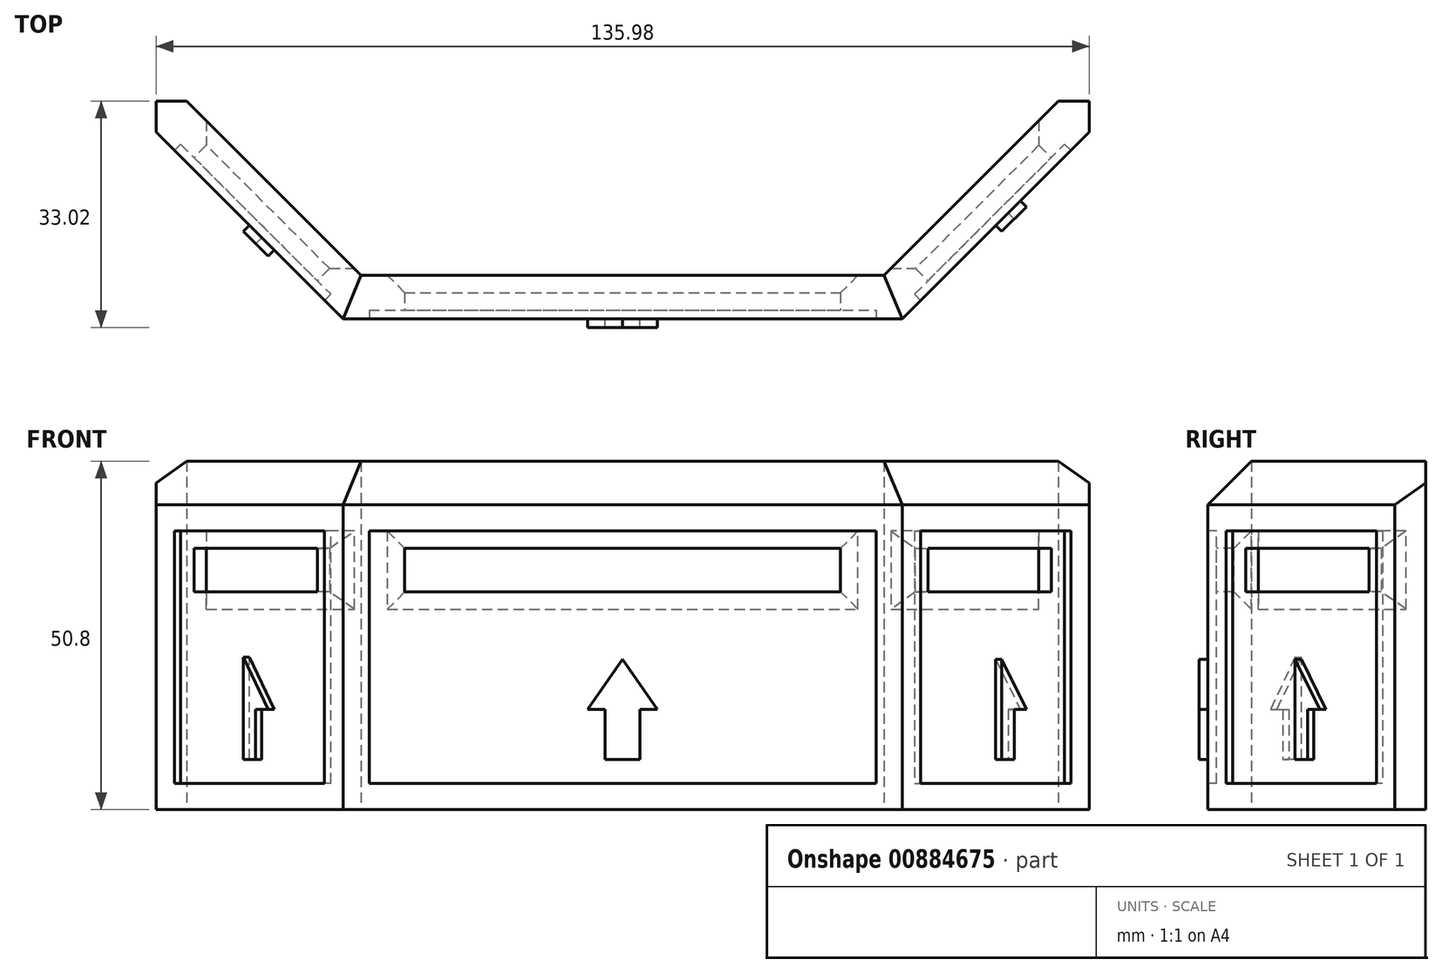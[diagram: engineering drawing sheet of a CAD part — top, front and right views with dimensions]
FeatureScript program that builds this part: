
annotation { "Feature Type Name" : "Feature", "Feature Type Description" : "" }
export const myFeature = defineFeature(function(context is Context, id is Id, definition is map)
    precondition{}
    {
        {
            var Q0;
            Q0=qCreatedBy(makeId("Top.planeOp"),FACE);
            var sketch = newSketch(context, id + "F0", { "sketchPlane" : qUnion([Q0])});
            skLineSegment(sketch, "E0", {"start": v(38.1, 0) * mm, "end": v(-38.1, 0) * mm});
            skLineSegment(sketch, "E1", {"start": v(-38.1, 0) * mm, "end": v(-63.5, 25.4) * mm});
            skLineSegment(sketch, "E2", {"start": v(38.1, 0) * mm, "end": v(63.5, 25.4) * mm});
            skPoint(sketch, "E3.start.orphan", {"position": v(0, 0) * mm});
            skLineSegment(sketch, "E4.0", {"start": v(42.6, -4.5) * mm, "end": v(68, 20.9) * mm});
            skLineSegment(sketch, "E5.0", {"start": v(-42.6, -4.5) * mm, "end": v(-68, 20.9) * mm});
            skLineSegment(sketch, "E6", {"start": v(-42.6, -4.5) * mm, "end": v(-40.73, -6.35) * mm});
            skLineSegment(sketch, "E7", {"start": v(-38.1, -6.35) * mm, "end": v(-40.73, -6.35) * mm});
            skLineSegment(sketch, "E8", {"start": v(-38.1, -6.35) * mm, "end": v(40.73, -6.35) * mm});
            skLineSegment(sketch, "E9", {"start": v(42.6, -4.5) * mm, "end": v(40.73, -6.35) * mm});
            skLineSegment(sketch, "E10", {"start": v(-68, 20.9) * mm, "end": v(-68, 25.4) * mm});
            skLineSegment(sketch, "E11", {"start": v(-63.5, 25.4) * mm, "end": v(-68, 25.4) * mm});
            skLineSegment(sketch, "E12", {"start": v(-68, 25.4) * mm, "end": v(-63.5, 25.4) * mm});
            skLineSegment(sketch, "E13", {"start": v(68, 20.9) * mm, "end": v(68, 25.4) * mm});
            skLineSegment(sketch, "E14.trimOffspring", {"start": v(63.5, 25.4) * mm, "end": v(68, 25.4) * mm});
            skSolve(sketch);
        }
        {
            var Q0;
            Q0=qSketchRegion(id+"F0",true);
            extrude(context, id + "F1", {"entities" : qUnion([Q0]), "depth" : 50.8 * mm, "offsetDistance" : 25.4 * mm});
        }
        {
            var Q0;
            Q0=makeQuery(id+"F1.opExtrude","CAP_EDGE",EDGE,{"disambiguationData":[OSD([sQuery(id+"F0.wireOp",EDGE,"E5.0"),sQuery(id+"F0.wireOp",EDGE,"E6")])],"isStart":false});
            var Q1;
            Q1=makeQuery(id+"F1.opExtrude","CAP_EDGE",EDGE,{"disambiguationData":[OSD([sQuery(id+"F0.wireOp",EDGE,"E7"),sQuery(id+"F0.wireOp",EDGE,"E8")])],"isStart":false});
            var Q2;
            Q2=makeQuery(id+"F1.opExtrude","CAP_EDGE",EDGE,{"disambiguationData":[OSD([sQuery(id+"F0.wireOp",EDGE,"E4.0"),sQuery(id+"F0.wireOp",EDGE,"E9")])],"isStart":false});
            chamfer(context, id + "F2", {"entities" : qUnion([Q0, Q1, Q2]), "chamferType" : ChamferType.OFFSET_ANGLE, "width" : 6.35 * mm, "oppositeDirection" : false, "angle" : 45 * degree, "tangentPropagation" : true});
        }
        {
            var Q0;
            Q0=makeQuery(id+"F1.opExtrude","SWEPT_FACE",FACE,{"disambiguationData":[OSD([sQuery(id+"F0.wireOp",EDGE,"E7"),sQuery(id+"F0.wireOp",EDGE,"E8")])]});
            var sketch = newSketch(context, id + "F3", { "sketchPlane" : qUnion([Q0])});
            skLineSegment(sketch, "E15", {"start": v(0, 0) * mm, "end": v(0, 31.75) * mm});
            skLineSegment(sketch, "E16", {"start": v(0, 31.75) * mm, "end": v(31.75, 31.75) * mm});
            skLineSegment(sketch, "E17", {"start": v(31.75, 31.75) * mm, "end": v(-31.75, 31.75) * mm});
            skLineSegment(sketch, "E18", {"start": v(0, 31.75) * mm, "end": v(0, 38.1) * mm});
            skLineSegment(sketch, "E19", {"start": v(0, 38.1) * mm, "end": v(31.75, 38.1) * mm});
            skLineSegment(sketch, "E20", {"start": v(31.75, 38.1) * mm, "end": v(-31.75, 38.1) * mm});
            skLineSegment(sketch, "E21", {"start": v(-31.75, 31.75) * mm, "end": v(-31.75, 38.1) * mm});
            skLineSegment(sketch, "E22", {"start": v(31.75, 31.75) * mm, "end": v(31.75, 38.1) * mm});
            skLineSegment(sketch, "E23", {"start": v(0, 31.75) * mm, "end": v(0, 29.21) * mm});
            skLineSegment(sketch, "E24", {"start": v(0, 29.21) * mm, "end": v(0, 0) * mm});
            skLineSegment(sketch, "E25", {"start": v(0, 14.6) * mm, "end": v(0, 29.21) * mm});
            skLineSegment(sketch, "E26", {"start": v(0, 14.6) * mm, "end": v(0, 0) * mm});
            skLineSegment(sketch, "E27", {"start": v(0, 7.3) * mm, "end": v(-2.54, 7.3) * mm});
            skLineSegment(sketch, "E28", {"start": v(-2.54, 7.3) * mm, "end": v(2.54, 7.3) * mm});
            skLineSegment(sketch, "E29", {"start": v(-2.54, 14.6) * mm, "end": v(-5.08, 14.6) * mm});
            skLineSegment(sketch, "E30", {"start": v(2.54, 14.6) * mm, "end": v(5.08, 14.6) * mm});
            skLineSegment(sketch, "E31", {"start": v(-5.08, 14.6) * mm, "end": v(0, 21.9) * mm});
            skLineSegment(sketch, "E32", {"start": v(0, 21.9) * mm, "end": v(5.08, 14.6) * mm});
            skLineSegment(sketch, "E33", {"start": v(-2.54, 14.6) * mm, "end": v(-2.54, 7.3) * mm});
            skLineSegment(sketch, "E34", {"start": v(2.54, 14.6) * mm, "end": v(2.54, 7.3) * mm});
            skSolve(sketch);
        }
        {
            var Q0;
            {var subQ2=sQuery(id+"F3.wireOp",EDGE,"E18");Q0=makeQuery(id+"F3.imprint","IMPRINT",FACE,{"disambiguationData":[TD([[makeQuery(id+"F3.imprint","IMPRINT",EDGE,{"derivedFrom":subQ2}),-1.0]])]});}
            var Q1;
            {var subQ2=sQuery(id+"F3.wireOp",EDGE,"E18");Q1=makeQuery(id+"F3.imprint","IMPRINT",FACE,{"disambiguationData":[TD([[makeQuery(id+"F3.imprint","IMPRINT",EDGE,{"derivedFrom":subQ2}),1.0]])]});}
            extrude(context, id + "F4", {"entities" : qUnion([Q0, Q1]), "operationType" : NewBodyOperationType.REMOVE, "oppositeDirection" : true, "depth" : 25.4 * mm, "offsetDistance" : 25.4 * mm});
        }
        {
            var Q0;
            Q0=makeQuery(id+"F4.boolean.opBoolean","COPY",EDGE,{"derivedFrom":makeQuery(id+"F4.opExtrude","CAP_EDGE",EDGE,{"disambiguationData":[OSD([sQuery(id+"F3.wireOp",EDGE,"E17")])],"isStart":true})});
            var Q1;
            Q1=makeQuery(id+"F4.boolean.opBoolean","COPY",EDGE,{"derivedFrom":makeQuery(id+"F4.opExtrude","CAP_EDGE",EDGE,{"disambiguationData":[OSD([sQuery(id+"F3.wireOp",EDGE,"E21")])],"isStart":true})});
            var Q2;
            Q2=makeQuery(id+"F4.boolean.opBoolean","COPY",EDGE,{"derivedFrom":makeQuery(id+"F4.opExtrude","CAP_EDGE",EDGE,{"disambiguationData":[OSD([sQuery(id+"F3.wireOp",EDGE,"E20")])],"isStart":true})});
            var Q3;
            Q3=makeQuery(id+"F4.boolean.opBoolean","COPY",EDGE,{"derivedFrom":makeQuery(id+"F4.opExtrude","CAP_EDGE",EDGE,{"disambiguationData":[OSD([sQuery(id+"F3.wireOp",EDGE,"E22")])],"isStart":true})});
            var Q4;
            Q4=makeQuery(id+"F4.boolean.opBoolean","INTERSECT",EDGE,{"derivedFrom":[makeQuery(id+"F1.opExtrude","SWEPT_FACE",FACE,{"disambiguationData":[OSD([sQuery(id+"F0.wireOp",EDGE,"E0")])]}),makeQuery(id+"F4.opExtrude","SWEPT_FACE",FACE,{"disambiguationData":[OSD([sQuery(id+"F3.wireOp",EDGE,"E21")])]})]});
            var Q5;
            Q5=makeQuery(id+"F4.boolean.opBoolean","INTERSECT",EDGE,{"derivedFrom":[makeQuery(id+"F1.opExtrude","SWEPT_FACE",FACE,{"disambiguationData":[OSD([sQuery(id+"F0.wireOp",EDGE,"E0")])]}),makeQuery(id+"F4.opExtrude","SWEPT_FACE",FACE,{"disambiguationData":[OSD([sQuery(id+"F3.wireOp",EDGE,"E20")])]})]});
            var Q6;
            Q6=makeQuery(id+"F4.boolean.opBoolean","INTERSECT",EDGE,{"derivedFrom":[makeQuery(id+"F1.opExtrude","SWEPT_FACE",FACE,{"disambiguationData":[OSD([sQuery(id+"F0.wireOp",EDGE,"E0")])]}),makeQuery(id+"F4.opExtrude","SWEPT_FACE",FACE,{"disambiguationData":[OSD([sQuery(id+"F3.wireOp",EDGE,"E17")])]})]});
            var Q7;
            Q7=makeQuery(id+"F4.boolean.opBoolean","INTERSECT",EDGE,{"derivedFrom":[makeQuery(id+"F1.opExtrude","SWEPT_FACE",FACE,{"disambiguationData":[OSD([sQuery(id+"F0.wireOp",EDGE,"E0")])]}),makeQuery(id+"F4.opExtrude","SWEPT_FACE",FACE,{"disambiguationData":[OSD([sQuery(id+"F3.wireOp",EDGE,"E22")])]})]});
            chamfer(context, id + "F5", {"entities" : qUnion([Q0, Q1, Q2, Q3, Q4, Q5, Q6, Q7]), "width" : 2.54 * mm, "tangentPropagation" : true});
        }
        {
            var Q0;
            Q0=makeQuery(id+"F1.opExtrude","SWEPT_FACE",FACE,{"disambiguationData":[OSD([sQuery(id+"F0.wireOp",EDGE,"E5.0"),sQuery(id+"F0.wireOp",EDGE,"E6")])]});
            var sketch = newSketch(context, id + "F6", { "sketchPlane" : qUnion([Q0])});
            skLineSegment(sketch, "E35", {"start": v(-47.4, 31.75) * mm, "end": v(-30.89, 31.75) * mm});
            skLineSegment(sketch, "E36", {"start": v(-30.89, 31.75) * mm, "end": v(-56.29, 31.75) * mm});
            skLineSegment(sketch, "E37", {"start": v(-30.89, 31.75) * mm, "end": v(-30.89, 38.1) * mm});
            skLineSegment(sketch, "E38", {"start": v(-39.78, 38.1) * mm, "end": v(-30.89, 38.1) * mm});
            skLineSegment(sketch, "E39", {"start": v(-30.89, 38.1) * mm, "end": v(-56.29, 38.1) * mm});
            skLineSegment(sketch, "E40", {"start": v(-56.29, 31.75) * mm, "end": v(-56.29, 38.1) * mm});
            skPoint(sketch, "E41.start.orphan", {"position": v(-43.59, 0) * mm});
            skLineSegment(sketch, "E42", {"start": v(-43.59, 0) * mm, "end": v(-43.59, 44.45) * mm});
            skLineSegment(sketch, "E43", {"start": v(-43.59, 44.45) * mm, "end": v(-43.59, 31.75) * mm});
            skLineSegment(sketch, "E44", {"start": v(-43.59, 31.75) * mm, "end": v(-43.59, 29.21) * mm});
            skLineSegment(sketch, "E45", {"start": v(-43.59, 29.21) * mm, "end": v(-43.59, 0) * mm});
            skLineSegment(sketch, "E46", {"start": v(-43.59, 14.6) * mm, "end": v(-43.59, 29.21) * mm});
            skLineSegment(sketch, "E47", {"start": v(-43.59, 14.6) * mm, "end": v(-43.59, 0) * mm});
            skLineSegment(sketch, "E48", {"start": v(-46.13, 14.6) * mm, "end": v(-48.67, 14.6) * mm});
            skLineSegment(sketch, "E49", {"start": v(-48.67, 14.6) * mm, "end": v(-46.13, 14.6) * mm});
            skLineSegment(sketch, "E50", {"start": v(-43.59, 22.23) * mm, "end": v(-48.67, 14.6) * mm});
            skLineSegment(sketch, "E51", {"start": v(-43.59, 22.23) * mm, "end": v(-38.5, 14.6) * mm});
            skLineSegment(sketch, "E52", {"start": v(-46.13, 14.6) * mm, "end": v(-46.13, 7.3) * mm});
            skLineSegment(sketch, "E53", {"start": v(-38.5, 14.6) * mm, "end": v(-41.05, 14.6) * mm});
            skLineSegment(sketch, "E54", {"start": v(-41.05, 14.6) * mm, "end": v(-41.05, 7.3) * mm});
            skLineSegment(sketch, "E55", {"start": v(-43.59, 7.3) * mm, "end": v(-41.05, 7.3) * mm});
            skLineSegment(sketch, "E56", {"start": v(-41.05, 7.3) * mm, "end": v(-46.13, 7.3) * mm});
            skLineSegment(sketch, "E57.trimOffspring", {"start": v(-41.05, 14.6) * mm, "end": v(-38.5, 14.6) * mm});
            skSolve(sketch);
        }
        {
            var Q0;
            {var subQ1=sQuery(id+"F6.wireOp",EDGE,"E37");Q0=makeQuery(id+"F6.imprint","IMPRINT",FACE,{"disambiguationData":[TD([[makeQuery(id+"F6.imprint","IMPRINT",EDGE,{"derivedFrom":subQ1}),1.0]])]});}
            var Q1;
            {var subQ0=sQuery(id+"F6.wireOp",EDGE,"E40");Q1=makeQuery(id+"F6.imprint","IMPRINT",FACE,{"disambiguationData":[TD([[makeQuery(id+"F6.imprint","IMPRINT",EDGE,{"derivedFrom":subQ0}),-1.0]])]});}
            extrude(context, id + "F7", {"entities" : qUnion([Q0, Q1]), "operationType" : NewBodyOperationType.REMOVE, "oppositeDirection" : true, "depth" : 25.4 * mm, "offsetDistance" : 25.4 * mm});
        }
        {
            var Q0;
            Q0=makeQuery(id+"F7.boolean.opBoolean","COPY",EDGE,{"derivedFrom":makeQuery(id+"F7.opExtrude","CAP_EDGE",EDGE,{"disambiguationData":[OSD([sQuery(id+"F6.wireOp",EDGE,"E39")])],"isStart":true})});
            var Q1;
            Q1=makeQuery(id+"F7.boolean.opBoolean","COPY",EDGE,{"derivedFrom":makeQuery(id+"F7.opExtrude","CAP_EDGE",EDGE,{"disambiguationData":[OSD([sQuery(id+"F6.wireOp",EDGE,"E37")])],"isStart":true})});
            var Q2;
            Q2=makeQuery(id+"F7.boolean.opBoolean","COPY",EDGE,{"derivedFrom":makeQuery(id+"F7.opExtrude","CAP_EDGE",EDGE,{"disambiguationData":[OSD([sQuery(id+"F6.wireOp",EDGE,"E36")])],"isStart":true})});
            var Q3;
            Q3=makeQuery(id+"F7.boolean.opBoolean","COPY",EDGE,{"derivedFrom":makeQuery(id+"F7.opExtrude","CAP_EDGE",EDGE,{"disambiguationData":[OSD([sQuery(id+"F6.wireOp",EDGE,"E40")])],"isStart":true})});
            var Q4;
            Q4=makeQuery(id+"F7.boolean.opBoolean","INTERSECT",EDGE,{"derivedFrom":[makeQuery(id+"F1.opExtrude","SWEPT_FACE",FACE,{"disambiguationData":[OSD([sQuery(id+"F0.wireOp",EDGE,"E1")])]}),makeQuery(id+"F7.opExtrude","SWEPT_FACE",FACE,{"disambiguationData":[OSD([sQuery(id+"F6.wireOp",EDGE,"E39")])]})]});
            var Q5;
            Q5=makeQuery(id+"F7.boolean.opBoolean","INTERSECT",EDGE,{"derivedFrom":[makeQuery(id+"F1.opExtrude","SWEPT_FACE",FACE,{"disambiguationData":[OSD([sQuery(id+"F0.wireOp",EDGE,"E1")])]}),makeQuery(id+"F7.opExtrude","SWEPT_FACE",FACE,{"disambiguationData":[OSD([sQuery(id+"F6.wireOp",EDGE,"E37")])]})]});
            var Q6;
            Q6=makeQuery(id+"F7.boolean.opBoolean","INTERSECT",EDGE,{"derivedFrom":[makeQuery(id+"F1.opExtrude","SWEPT_FACE",FACE,{"disambiguationData":[OSD([sQuery(id+"F0.wireOp",EDGE,"E1")])]}),makeQuery(id+"F7.opExtrude","SWEPT_FACE",FACE,{"disambiguationData":[OSD([sQuery(id+"F6.wireOp",EDGE,"E36")])]})]});
            var Q7;
            Q7=makeQuery(id+"F7.boolean.opBoolean","INTERSECT",EDGE,{"derivedFrom":[makeQuery(id+"F1.opExtrude","SWEPT_FACE",FACE,{"disambiguationData":[OSD([sQuery(id+"F0.wireOp",EDGE,"E1")])]}),makeQuery(id+"F7.opExtrude","SWEPT_FACE",FACE,{"disambiguationData":[OSD([sQuery(id+"F6.wireOp",EDGE,"E40")])]})]});
            chamfer(context, id + "F8", {"entities" : qUnion([Q0, Q1, Q2, Q3, Q4, Q5, Q6, Q7]), "width" : 2.54 * mm, "tangentPropagation" : true});
        }
        {
            var Q0;
            Q0=makeQuery(id+"F1.opExtrude","SWEPT_FACE",FACE,{"disambiguationData":[OSD([sQuery(id+"F0.wireOp",EDGE,"E4.0"),sQuery(id+"F0.wireOp",EDGE,"E9")])]});
            var sketch = newSketch(context, id + "F9", { "sketchPlane" : qUnion([Q0])});
            skLineSegment(sketch, "E58", {"start": v(30.89, 31.75) * mm, "end": v(56.29, 31.75) * mm});
            skLineSegment(sketch, "E59", {"start": v(43.59, 38.1) * mm, "end": v(56.29, 38.1) * mm});
            skLineSegment(sketch, "E60", {"start": v(56.29, 38.1) * mm, "end": v(30.89, 38.1) * mm});
            skLineSegment(sketch, "E61", {"start": v(30.89, 31.75) * mm, "end": v(30.89, 38.1) * mm});
            skLineSegment(sketch, "E62", {"start": v(56.29, 31.75) * mm, "end": v(56.29, 38.1) * mm});
            skPoint(sketch, "E63.end.orphan", {"position": v(43.59, 31.75) * mm});
            skPoint(sketch, "E63.start.orphan", {"position": v(43.59, 0) * mm});
            skLineSegment(sketch, "E64", {"start": v(43.59, 0) * mm, "end": v(43.59, 44.45) * mm});
            skLineSegment(sketch, "E65", {"start": v(43.59, 44.45) * mm, "end": v(43.59, 31.75) * mm});
            skLineSegment(sketch, "E66", {"start": v(43.59, 31.75) * mm, "end": v(43.59, 29.21) * mm});
            skLineSegment(sketch, "E67", {"start": v(43.59, 29.21) * mm, "end": v(43.59, 0) * mm});
            skLineSegment(sketch, "E68", {"start": v(43.59, 14.6) * mm, "end": v(43.59, 29.21) * mm});
            skLineSegment(sketch, "E69", {"start": v(43.59, 14.6) * mm, "end": v(43.59, 0) * mm});
            skLineSegment(sketch, "E70", {"start": v(41.05, 14.6) * mm, "end": v(38.5, 14.6) * mm});
            skLineSegment(sketch, "E71", {"start": v(38.5, 14.6) * mm, "end": v(41.05, 14.6) * mm});
            skLineSegment(sketch, "E72", {"start": v(43.59, 21.9) * mm, "end": v(38.5, 14.6) * mm});
            skLineSegment(sketch, "E73", {"start": v(43.59, 21.9) * mm, "end": v(48.67, 14.6) * mm});
            skLineSegment(sketch, "E74", {"start": v(41.05, 14.6) * mm, "end": v(41.05, 7.3) * mm});
            skLineSegment(sketch, "E75", {"start": v(46.13, 14.6) * mm, "end": v(48.67, 14.6) * mm});
            skLineSegment(sketch, "E76", {"start": v(46.13, 14.6) * mm, "end": v(46.13, 7.3) * mm});
            skLineSegment(sketch, "E77", {"start": v(43.59, 7.3) * mm, "end": v(46.13, 7.3) * mm});
            skLineSegment(sketch, "E78", {"start": v(46.13, 7.3) * mm, "end": v(41.05, 7.3) * mm});
            skPoint(sketch, "E79.orphan", {"position": v(41.05, 6.33) * mm});
            skSolve(sketch);
        }
        {
            var Q0;
            {var subQ0=sQuery(id+"F9.wireOp",EDGE,"E61");Q0=makeQuery(id+"F9.imprint","IMPRINT",FACE,{"disambiguationData":[TD([[makeQuery(id+"F9.imprint","IMPRINT",EDGE,{"derivedFrom":subQ0}),-1.0]])]});}
            var Q1;
            {var subQ0=sQuery(id+"F9.wireOp",EDGE,"E62");Q1=makeQuery(id+"F9.imprint","IMPRINT",FACE,{"disambiguationData":[TD([[makeQuery(id+"F9.imprint","IMPRINT",EDGE,{"derivedFrom":subQ0}),1.0]])]});}
            extrude(context, id + "F10", {"entities" : qUnion([Q0, Q1]), "operationType" : NewBodyOperationType.REMOVE, "oppositeDirection" : true, "depth" : 25.4 * mm, "offsetDistance" : 25.4 * mm});
        }
        {
            var Q0;
            Q0=makeQuery(id+"F10.boolean.opBoolean","COPY",EDGE,{"derivedFrom":makeQuery(id+"F10.opExtrude","CAP_EDGE",EDGE,{"disambiguationData":[OSD([sQuery(id+"F9.wireOp",EDGE,"E60")])],"isStart":true})});
            var Q1;
            Q1=makeQuery(id+"F10.boolean.opBoolean","COPY",EDGE,{"derivedFrom":makeQuery(id+"F10.opExtrude","CAP_EDGE",EDGE,{"disambiguationData":[OSD([sQuery(id+"F9.wireOp",EDGE,"E61")])],"isStart":true})});
            var Q2;
            Q2=makeQuery(id+"F10.boolean.opBoolean","COPY",EDGE,{"derivedFrom":makeQuery(id+"F10.opExtrude","CAP_EDGE",EDGE,{"disambiguationData":[OSD([sQuery(id+"F9.wireOp",EDGE,"E58")])],"isStart":true})});
            var Q3;
            Q3=makeQuery(id+"F10.boolean.opBoolean","COPY",EDGE,{"derivedFrom":makeQuery(id+"F10.opExtrude","CAP_EDGE",EDGE,{"disambiguationData":[OSD([sQuery(id+"F9.wireOp",EDGE,"E62")])],"isStart":true})});
            var Q4;
            Q4=makeQuery(id+"F10.boolean.opBoolean","INTERSECT",EDGE,{"derivedFrom":[makeQuery(id+"F1.opExtrude","SWEPT_FACE",FACE,{"disambiguationData":[OSD([sQuery(id+"F0.wireOp",EDGE,"E2")])]}),makeQuery(id+"F10.opExtrude","SWEPT_FACE",FACE,{"disambiguationData":[OSD([sQuery(id+"F9.wireOp",EDGE,"E61")])]})]});
            var Q5;
            Q5=makeQuery(id+"F10.boolean.opBoolean","INTERSECT",EDGE,{"derivedFrom":[makeQuery(id+"F1.opExtrude","SWEPT_FACE",FACE,{"disambiguationData":[OSD([sQuery(id+"F0.wireOp",EDGE,"E2")])]}),makeQuery(id+"F10.opExtrude","SWEPT_FACE",FACE,{"disambiguationData":[OSD([sQuery(id+"F9.wireOp",EDGE,"E60")])]})]});
            var Q6;
            Q6=makeQuery(id+"F10.boolean.opBoolean","INTERSECT",EDGE,{"derivedFrom":[makeQuery(id+"F1.opExtrude","SWEPT_FACE",FACE,{"disambiguationData":[OSD([sQuery(id+"F0.wireOp",EDGE,"E2")])]}),makeQuery(id+"F10.opExtrude","SWEPT_FACE",FACE,{"disambiguationData":[OSD([sQuery(id+"F9.wireOp",EDGE,"E58")])]})]});
            var Q7;
            Q7=makeQuery(id+"F10.boolean.opBoolean","INTERSECT",EDGE,{"derivedFrom":[makeQuery(id+"F1.opExtrude","SWEPT_FACE",FACE,{"disambiguationData":[OSD([sQuery(id+"F0.wireOp",EDGE,"E2")])]}),makeQuery(id+"F10.opExtrude","SWEPT_FACE",FACE,{"disambiguationData":[OSD([sQuery(id+"F9.wireOp",EDGE,"E62")])]})]});
            chamfer(context, id + "F11", {"entities" : qUnion([Q0, Q1, Q2, Q3, Q4, Q5, Q6, Q7]), "width" : 2.54 * mm, "tangentPropagation" : true});
        }
        {
            var Q0;
            Q0=makeQuery(id+"F1.opExtrude","SWEPT_FACE",FACE,{"disambiguationData":[OSD([sQuery(id+"F0.wireOp",EDGE,"E7"),sQuery(id+"F0.wireOp",EDGE,"E8")])]});
            var sketch = newSketch(context, id + "F12", { "sketchPlane" : qUnion([Q0])});
            skLineSegment(sketch, "E80.0", {"start": v(36.92, 3.81) * mm, "end": v(36.92, 40.64) * mm});
            skLineSegment(sketch, "E80.1", {"start": v(-36.92, 3.81) * mm, "end": v(36.92, 3.81) * mm});
            skLineSegment(sketch, "E80.2", {"start": v(-36.92, 40.64) * mm, "end": v(-36.92, 3.81) * mm});
            skLineSegment(sketch, "E80.3", {"start": v(36.92, 40.64) * mm, "end": v(-36.92, 40.64) * mm});
            skSolve(sketch);
        }
        {
            var Q0;
            Q0=makeQuery(id+"F1.opExtrude","SWEPT_FACE",FACE,{"disambiguationData":[OSD([sQuery(id+"F0.wireOp",EDGE,"E5.0"),sQuery(id+"F0.wireOp",EDGE,"E6")])]});
            var sketch = newSketch(context, id + "F13", { "sketchPlane" : qUnion([Q0])});
            skLineSegment(sketch, "E81.0", {"start": v(-28.12, 3.81) * mm, "end": v(-28.12, 40.64) * mm});
            skLineSegment(sketch, "E81.1", {"start": v(-59.05, 3.81) * mm, "end": v(-28.12, 3.81) * mm});
            skLineSegment(sketch, "E81.2", {"start": v(-59.05, 40.64) * mm, "end": v(-59.05, 3.81) * mm});
            skLineSegment(sketch, "E81.3", {"start": v(-28.12, 40.64) * mm, "end": v(-59.05, 40.64) * mm});
            skSolve(sketch);
        }
        {
            var Q0;
            Q0=makeQuery(id+"F1.opExtrude","SWEPT_FACE",FACE,{"disambiguationData":[OSD([sQuery(id+"F0.wireOp",EDGE,"E4.0"),sQuery(id+"F0.wireOp",EDGE,"E9")])]});
            var sketch = newSketch(context, id + "F14", { "sketchPlane" : qUnion([Q0])});
            skLineSegment(sketch, "E82.0", {"start": v(59.05, 3.81) * mm, "end": v(59.05, 40.64) * mm});
            skLineSegment(sketch, "E82.1", {"start": v(28.12, 3.81) * mm, "end": v(59.05, 3.81) * mm});
            skLineSegment(sketch, "E82.2", {"start": v(28.12, 40.64) * mm, "end": v(28.12, 3.81) * mm});
            skLineSegment(sketch, "E82.3", {"start": v(59.05, 40.64) * mm, "end": v(28.12, 40.64) * mm});
            skSolve(sketch);
        }
        {
            var Q0;
            {var subQ4=sQuery(id+"F12.wireOp",EDGE,"E80.0");Q0=makeQuery(id+"F12.imprint","IMPRINT",FACE,{"disambiguationData":[TD([[makeQuery(id+"F12.imprint","IMPRINT",EDGE,{"derivedFrom":subQ4}),1.0]])]});}
            extrude(context, id + "F15", {"entities" : qUnion([Q0]), "operationType" : NewBodyOperationType.REMOVE, "oppositeDirection" : true, "depth" : 1.27 * mm, "offsetDistance" : 25.4 * mm});
        }
        {
            var Q0;
            {var subQ3=sQuery(id+"F13.wireOp",EDGE,"E81.0");Q0=makeQuery(id+"F13.imprint","IMPRINT",FACE,{"disambiguationData":[TD([[makeQuery(id+"F13.imprint","IMPRINT",EDGE,{"derivedFrom":subQ3}),1.0]])]});}
            extrude(context, id + "F16", {"entities" : qUnion([Q0]), "operationType" : NewBodyOperationType.REMOVE, "oppositeDirection" : true, "depth" : 1.27 * mm, "offsetDistance" : 25.4 * mm});
        }
        {
            var Q0;
            {var subQ3=sQuery(id+"F14.wireOp",EDGE,"E82.0");Q0=makeQuery(id+"F14.imprint","IMPRINT",FACE,{"disambiguationData":[TD([[makeQuery(id+"F14.imprint","IMPRINT",EDGE,{"derivedFrom":subQ3}),1.0]])]});}
            extrude(context, id + "F17", {"entities" : qUnion([Q0]), "operationType" : NewBodyOperationType.REMOVE, "oppositeDirection" : true, "depth" : 1.27 * mm, "offsetDistance" : 25.4 * mm});
        }
        {
            var Q0;
            Q0=makeQuery(id+"F3.imprint","IMPRINT",FACE,{"disambiguationData":[TD([[makeQuery(id+"F3.imprint","IMPRINT",EDGE,{"derivedFrom":sQuery(id+"F3.wireOp",EDGE,"E30")}),1.0]])]});
            var Q1;
            Q1=makeQuery(id+"F3.imprint","IMPRINT",FACE,{"disambiguationData":[TD([[makeQuery(id+"F3.imprint","IMPRINT",EDGE,{"derivedFrom":sQuery(id+"F3.wireOp",EDGE,"E29")}),-1.0]])]});
            extrude(context, id + "F18", {"entities" : qUnion([Q0, Q1]), "depth" : 1.27 * mm, "offsetDistance" : 25.4 * mm});
        }
        {
            var Q0;
            {var subQ1=sQuery(id+"F9.wireOp",EDGE,"E73");Q0=makeQuery(id+"F9.imprint","IMPRINT",FACE,{"disambiguationData":[TD([[makeQuery(id+"F9.imprint","IMPRINT",EDGE,{"derivedFrom":subQ1}),-1.0]])]});}
            var Q1;
            Q1=makeQuery(id+"F9.imprint","IMPRINT",FACE,{"disambiguationData":[TD([[makeQuery(id+"F9.imprint","IMPRINT",EDGE,{"derivedFrom":sQuery(id+"F9.wireOp",EDGE,"E71")}),1.0]])]});
            extrude(context, id + "F19", {"entities" : qUnion([Q0, Q1]), "depth" : 1.27 * mm, "offsetDistance" : 25.4 * mm});
        }
        {
            var Q0;
            {var subQ1=sQuery(id+"F6.wireOp",EDGE,"E51");Q0=makeQuery(id+"F6.imprint","IMPRINT",FACE,{"disambiguationData":[TD([[makeQuery(id+"F6.imprint","IMPRINT",EDGE,{"derivedFrom":subQ1}),-1.0]])]});}
            var Q1;
            Q1=makeQuery(id+"F6.imprint","IMPRINT",FACE,{"disambiguationData":[TD([[makeQuery(id+"F6.imprint","IMPRINT",EDGE,{"derivedFrom":sQuery(id+"F6.wireOp",EDGE,"E49")}),1.0]])]});
            extrude(context, id + "F20", {"entities" : qUnion([Q0, Q1]), "depth" : 1.27 * mm, "offsetDistance" : 25.4 * mm});
        }
    });
